# Revit family: Layout-Teknion-Zones_Canteen_Tables_01-R2022
name_source: partatom
category: Furniture Systems
units: mm (PartAtom-declared; Revit-internal decimal feet)

## family parameters
Always vertical = Yes
Cut with Voids When Loaded = No
OmniClass Number = 23.40.70.14.64.21
OmniClass Title = Systems Furniture
Part Type = Normal
Room Calculation Point = No
Round Connector Dimension = Use Diameter
Shared = No
Work Plane-Based = No

## types (1)
- Canteen Tables 01
    Apparent Load = 0 VA
    Apparent Load Note = Complete With Canteen Table Type Information
    Assembly Code = E2020200
    Connector Description = Without Power Connector
    Default Elevation = 0' - 0"
    Depth = 6' - 4"
    Description = 6'-4" x 10'-3"
    Height = 3' - 6 15/16"
    Manufacturer = Teknion
    Manufacturer Fax = 416.661.4586
    Model = Canteen Tables 01
    Product Line = Zones
    Product Page URL = http://teknionplanningtool.com
    Series = Zones
    Sustainability Data = http://www.teknion.com
    URL = www.teknion.com
    Voltage = 0 V
    Voltage Note = Complete With Canteen Table Type Information
    Warranty = http://www.teknion.com
    Width = 10' - 3"

## geometry (parser evidence)
native form markers: Blend x44, Sweep x23
no freeform markers — native parametric forms only
